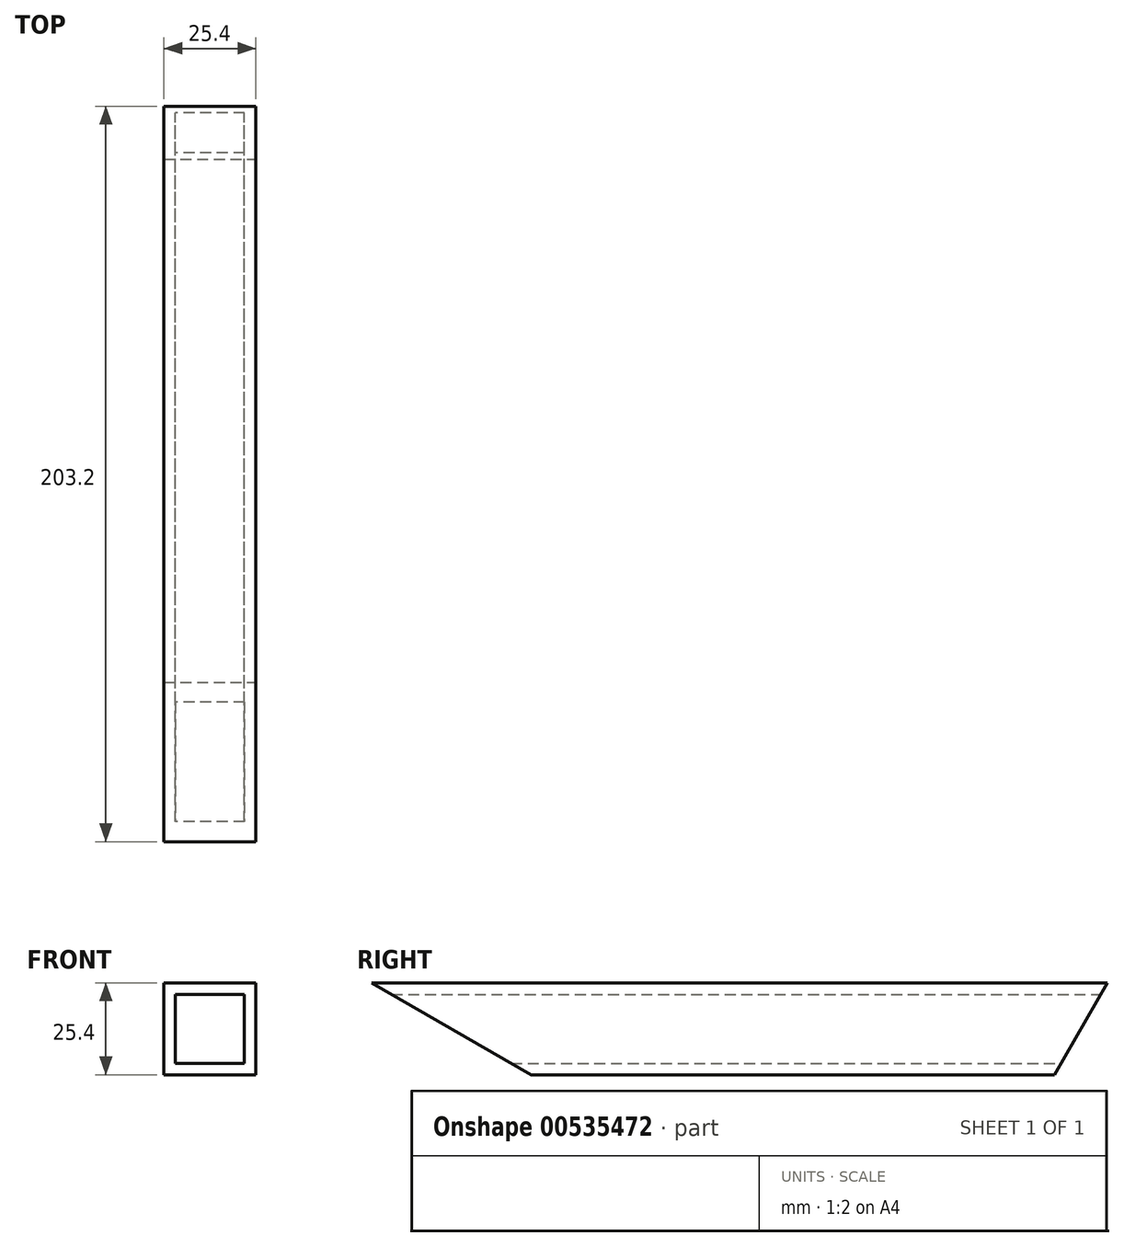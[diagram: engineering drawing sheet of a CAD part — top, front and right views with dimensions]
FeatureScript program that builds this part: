
annotation { "Feature Type Name" : "Feature", "Feature Type Description" : "" }
export const myFeature = defineFeature(function(context is Context, id is Id, definition is map)
    precondition{}
    {
        {
            var Q0;
            Q0=qCreatedBy(makeId("Front.planeOp"),FACE);
            var sketch = newSketch(context, id + "F0", { "sketchPlane" : qUnion([Q0])});
            skLineSegment(sketch, "E0.bottom", {"start": v(12.7, -12.7) * mm, "end": v(-12.7, -12.7) * mm});
            skLineSegment(sketch, "E0.top", {"start": v(12.7, 12.7) * mm, "end": v(-12.7, 12.7) * mm});
            skLineSegment(sketch, "E0.left", {"start": v(12.7, -12.7) * mm, "end": v(12.7, 12.7) * mm});
            skLineSegment(sketch, "E0.right", {"start": v(-12.7, -12.7) * mm, "end": v(-12.7, 12.7) * mm});
            skPoint(sketch, "E0.middle", {"position": v(0, 0) * mm});
            skLineSegment(sketch, "E1.bottom", {"start": v(9.53, -9.53) * mm, "end": v(-9.53, -9.53) * mm});
            skLineSegment(sketch, "E1.top", {"start": v(9.53, 9.53) * mm, "end": v(-9.53, 9.53) * mm});
            skLineSegment(sketch, "E1.left", {"start": v(9.53, -9.53) * mm, "end": v(9.53, 9.53) * mm});
            skLineSegment(sketch, "E1.right", {"start": v(-9.53, -9.53) * mm, "end": v(-9.53, 9.53) * mm});
            skSolve(sketch);
        }
        {
            var Q0;
            Q0=makeQuery(id+"F0.imprint","IMPRINT",FACE,{"disambiguationData":[TD([[makeQuery(id+"F0.imprint","IMPRINT",EDGE,{"derivedFrom":sQuery(id+"F0.wireOp",EDGE,"E0.bottom")}),-1.0]])]});
            extrude(context, id + "F1", {"entities" : qUnion([Q0]), "depth" : 203.2 * mm, "offsetDistance" : 25.4 * mm});
        }
        {
            var Q0;
            Q0=makeQuery(id+"F1.opExtrude","SWEPT_FACE",FACE,{"disambiguationData":[OSD([sQuery(id+"F0.wireOp",EDGE,"E0.left")])]});
            var sketch = newSketch(context, id + "F2", { "sketchPlane" : qUnion([Q0])});
            skLineSegment(sketch, "E2", {"start": v(-203.2, 12.7) * mm, "end": v(-159.2, -12.7) * mm});
            skLineSegment(sketch, "E3", {"start": v(0, 12.7) * mm, "end": v(-14.66, -12.7) * mm});
            skLineSegment(sketch, "E4", {"start": v(-203.2, 12.7) * mm, "end": v(-203.2, -12.7) * mm});
            skLineSegment(sketch, "E5", {"start": v(-203.2, -12.7) * mm, "end": v(-159.2, -12.7) * mm});
            skLineSegment(sketch, "E6", {"start": v(-14.66, -12.7) * mm, "end": v(0, -12.7) * mm});
            skLineSegment(sketch, "E7", {"start": v(0, -12.7) * mm, "end": v(0, 12.7) * mm});
            skSolve(sketch);
        }
        {
            var Q0;
            Q0=makeQuery(id+"F2.imprint","IMPRINT",FACE,{"disambiguationData":[TD([[makeQuery(id+"F2.imprint","IMPRINT",EDGE,{"derivedFrom":sQuery(id+"F2.wireOp",EDGE,"E2")}),-1.0]])]});
            var Q1;
            Q1=makeQuery(id+"F2.imprint","IMPRINT",FACE,{"disambiguationData":[TD([[makeQuery(id+"F2.imprint","IMPRINT",EDGE,{"derivedFrom":sQuery(id+"F2.wireOp",EDGE,"E3")}),1.0]])]});
            extrude(context, id + "F3", {"entities" : qUnion([Q0, Q1]), "operationType" : NewBodyOperationType.REMOVE, "endBound" : BoundingType.THROUGH_ALL, "oppositeDirection" : true, "depth" : 25.4 * mm, "offsetDistance" : 25.4 * mm});
        }
    });
